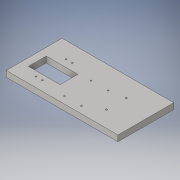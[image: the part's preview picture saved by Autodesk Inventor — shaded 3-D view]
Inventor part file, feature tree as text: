
AUTODESK INVENTOR PART (.ipt)
format: ipt  version: 2016 (Build 200138000, 138)  size: 157,184 bytes
history: native  units: in
note: dims shown in document units (in); Inventor stores cm internally (conversion verified against a paired STEP export)
features: extrude x5, sketch x5
ambient origin geometry x8: Origin, YZ Plane, XZ Plane, XY Plane, X Axis, Y Axis, Z Axis, Center Point
bodies: Solid1 (feature_tree)
feature tree (10):
  extrude  "RectangleFace"  Depth=5.5512in
  extrude  "RectangularCut"  Depth=0.5906in
  extrude  "AxleSupportHoles"  Depth=3.1496in
  extrude  "DriverHoles"  Depth=0.5906in TaperAngle=0.0deg
  extrude  "Extrusion5"  Depth=0.5906in
  sketch  "Sketch1"  dims[d0=11.1024in d1=5.5512in]
  sketch  "Sketch2"  dims[d2=0.5906in d3=0.0in d4=3.2126in]
  sketch  "Sketch3"  dims[d5=3.2283in d6=3.1496in]
  sketch  "Sketch4"  dims[d7=1.7717in d8=0.5906in d9=0.0in]
  sketch  "Sketch5"  dims[d10=0.7087in d11=0.4921in d12=0.315in d13=0.315in d14=0.315in d15=0.315in d16=0.1378in d17=0.1378in d18=0.1378in d19=0.1378in d20=0.5906in d21=0.0in d22=3.5433in d23=0.3937in d24=2.0079in d25=2.9724in d26=0.1575in d27=0.1575in d28=0.1575in d29=0.1575in d30=0.1575in d31=0.1575in d32=0.1575in d33=0.1575in d34=0.1378in d35=0.1378in d36=0.1378in d37=0.1378in d38=0.5906in d39=0.0in d40=2.7559in d41=1.9685in d42=1.9685in d43=0.1575in d44=0.1575in d45=0.5906in d46=0.0in]
